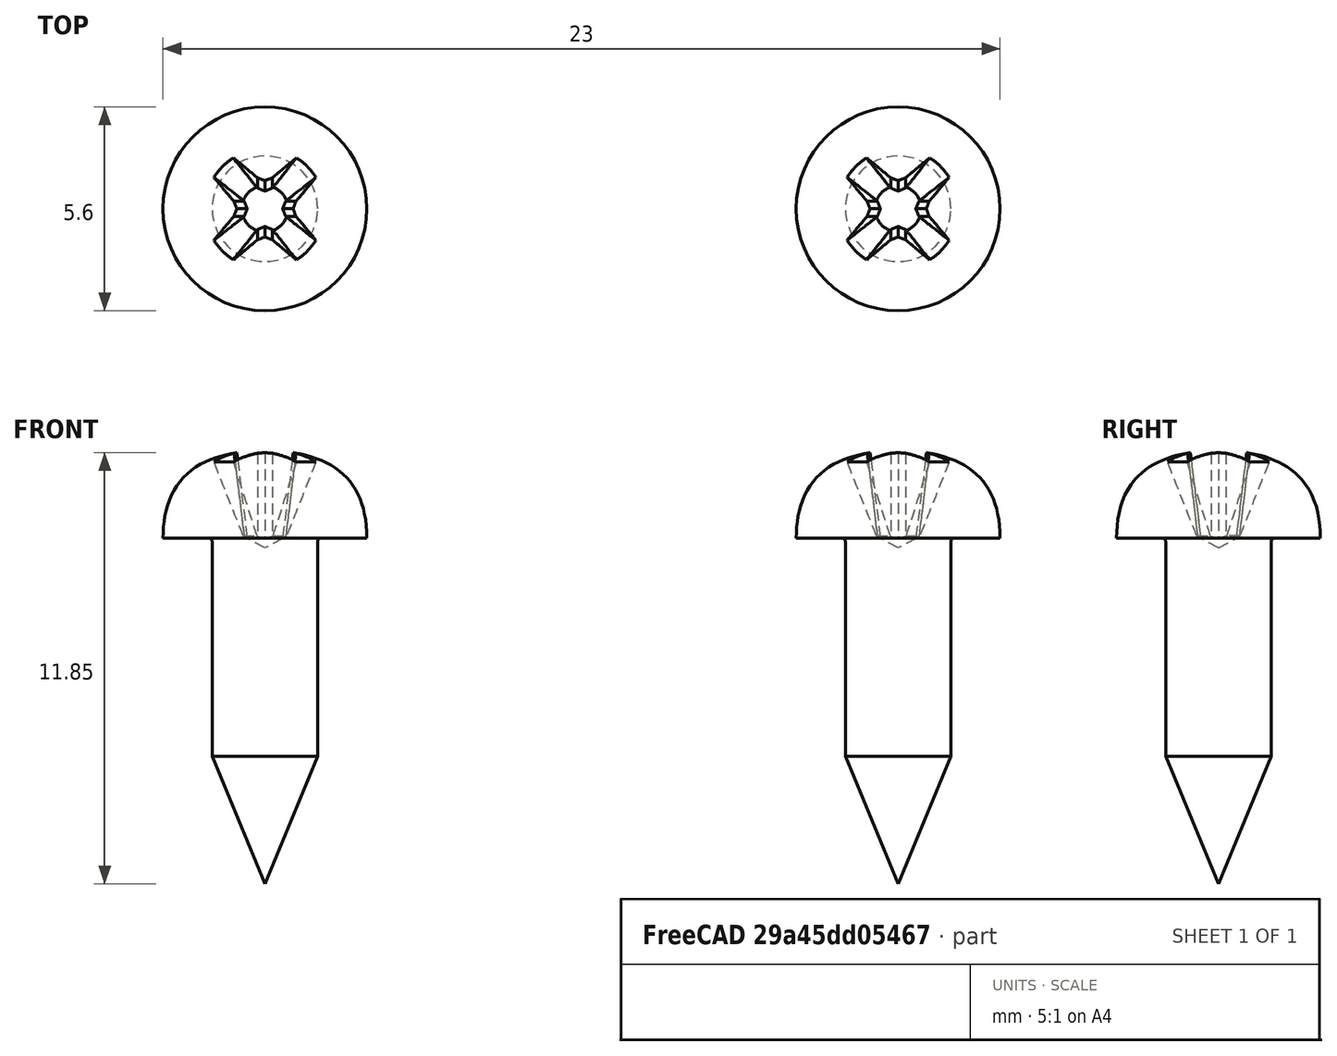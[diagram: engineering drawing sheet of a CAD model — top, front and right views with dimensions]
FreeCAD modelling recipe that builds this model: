
FCSTD DOCUMENT  (FreeCAD 1.0R39319 (Git))
Label: Assy_PiTracIRLED
License: All rights reserved
LicenseURL: https://en.wikipedia.org/wiki/All_rights_reserved
objects: TechDraw::DrawProjGroupItem×7, TechDraw::DrawViewBalloon×4, App::DocumentObjectGroup×3, App::Link×2, TechDraw::DrawSVGTemplate×2, Part::FeaturePython×2, TechDraw::DrawViewDimension×2, TechDraw::DrawPage×2, PartDesign::CoordinateSystem×1, App::FeaturePython×1, Spreadsheet::Sheet×1, TechDraw::DrawViewSpreadsheet×1, App::Part×1, TechDraw::DrawProjGroup×1
note: 6 computed .brp shape members not serialized (recipe doc carries the construction recipe); baked Part::Feature solids carry a one-line shape summary decoded from their .brp
EXTERNAL_REF file=../../Part/Print/5x2IRLED_Eyeball.FCStd obj=center
EXTERNAL_REF file=../../Part/Print/5x2IRLED_Eyeball.FCStd obj=Part
EXTERNAL_REF file=../../Part/Purchase/IRLED.FCStd obj=LCS_1
EXTERNAL_REF file=../../Part/Print/5x2IRLED_Eyeball.FCStd obj=LCS_1
EXTERNAL_REF file=../../Part/Purchase/IRLED.FCStd obj=IRLED_Only_1

FEATURE [App::DocumentObjectGroup] Parts
FEATURE [PartDesign::CoordinateSystem] LCS_Origin
  AttacherType = Attacher::AttachEngine3D
  AttachmentSupport = -> [X_Axis]
  MapMode = 2
FEATURE [App::DocumentObjectGroup] Constraints
FEATURE [App::FeaturePython] Variables  # WARN: FeaturePython — macro-defined, semantics opaque (R4)
  Type = App::PropertyContainer
FEATURE [App::DocumentObjectGroup] Configurations
FEATURE [App::Link] _x2IRLED_Eyeball  label="5x2IRLED_Eyeball"
  AttachedBy = #center
  AttachedTo = Parent Assembly#LCS_Origin
  LinkedObject = -> <external ../../Part/Print/5x2IRLED_Eyeball.FCStd>#Part
  SolverId = Asm4EE
  expr: Placement = LCS_Origin.Placement * AttachmentOffset * _x2IRLED_Eyeball#center.Placement ^ -1
FEATURE [App::Link] IRLED_Only_1  label="IRLED Only 1"
  AttachedBy = #LCS_1
  AttachedTo = _x2IRLED_Eyeball#LCS_1
  LinkPlacement = pos=(12.4672,17.5,0.0506) rot=(0,0,-1;1.5708rad)
  LinkedObject = -> <external ../../Part/Purchase/IRLED.FCStd>#IRLED_Only_1
  Placement = pos=(12.4672,17.5,0.0506) rot=(0,0,-1;1.5708rad)
  SolverId = Asm4EE
  expr: Placement = _x2IRLED_Eyeball.Placement * _x2IRLED_Eyeball#LCS_1.Placement * AttachmentOffset * IRLED#LCS_1.Placement ^ -1
FEATURE [TechDraw::DrawSVGTemplate] Template
  EditableTexts = approval_person=GitHub PR; creator=Stefan; date_of_issue=20.03.2026; document_type=Assembly Drawing; general_tolerances=na; identification_number=na; language_code=EN; part_material=na; revision_index=AAA; scale=1 : 1; sheet_number=1 / 1; title=Assy_PiTracIRLED
  Height = 297
  Orientation = 1
  Template = <userpath>/Documents/PiTrac/3D Printed Parts/Enclosure Version 3/Assets/PiTrac_A3_Landscape_ISO5457_minimal.svg
  Width = 420
FEATURE [Spreadsheet::Sheet] Spreadsheet  label="BOM"
  cells = A1=3; B1=2; C1='M3x10 mm self-tapping screw; D1='8-12 mm ; A2=2; B2=1; C2='5x2 IR LED board; D2='-; A3=1; B3=1; C3='5x2IRLED_Eyeball; D3='-; E3='PETG or PLA; A4='Position; B4='Quantity; C4='Part; D4='Dimensions; E4='Material
FEATURE [TechDraw::DrawViewSpreadsheet] Sheet
  CellEnd = E4
  CellStart = A1
  Font = osifont
  LineWidth = 0.35
  LockPosition = false
  Rotation = 0
  ScaleType = 2
  Source = -> Spreadsheet
  Symbol = <blob: 4584 chars omitted>
  TextSize = 12
  X = 324.475
  Y = 95.4404
FEATURE [Part::FeaturePython] Screw  label="ST2.9x9.5-Screw"  # WARN: FeaturePython — macro-defined, semantics opaque (R4)
  BaseObject = -> IRLED_Only_1 [Part__Feature067.Edge20]
  Diameter = 2
  Invert = false
  LeftHanded = false
  Length = 1
  LengthCustom = 9.5
  MatchOuter = false
  OffsetAngle = 0
  Placement = pos=(8.7,0,0.8124) rot=(0,0,1;0rad)
  Thread = false
  Type = 81
FEATURE [Part::FeaturePython] Screw001  label="ST2.9x9.5-Screw001"  # WARN: FeaturePython — macro-defined, semantics opaque (R4)
  BaseObject = -> IRLED_Only_1 [Part__Feature067.Edge17]
  Diameter = 2
  Invert = false
  LeftHanded = false
  Length = 1
  LengthCustom = 9.5
  MatchOuter = false
  OffsetAngle = 0
  Placement = pos=(-8.699,3.6e-15,0.8124) rot=(0,0,1;0rad)
  Thread = false
  Type = 81
FEATURE [App::Part] Assembly  label="Assy_PiTracIRLED"
  AssemblyType = Part::Link
  Group = -> [LCS_Origin,Constraints,Variables,Configurations,_x2IRLED_Eyeball,IRLED_Only_1,Screw,Screw001]
  Origin = -> Origin
  Type = Assembly
FEATURE [TechDraw::DrawProjGroupItem] ProjItem  label="Top"
  CoarseView = false
  Direction = (1,0,0)
  Focus = 100
  HardHidden = false
  IsoCount = 0
  IsoHidden = false
  IsoVisible = false
  LockPosition = false
  Perspective = false
  Rotation = 0
  RotationVector = (1,0,0)
  ScaleType = 0
  ScrubCount = 1
  SeamHidden = false
  SeamVisible = false
  SmoothHidden = false
  SmoothVisible = true
  Source = -> [Assembly]
  Type = 4
  X = 0
  XDirection = (0,-1,0)
  Y = -67
FEATURE [TechDraw::DrawProjGroupItem] View
  CoarseView = false
  Direction = (0.57735,-0.57735,0.57735)
  Focus = 100
  HardHidden = false
  IsoCount = 0
  IsoHidden = false
  IsoVisible = false
  LockPosition = false
  Perspective = false
  Rotation = 0
  RotationVector = (1,0,0)
  ScaleType = 0
  ScrubCount = 1
  SeamHidden = false
  SeamVisible = false
  SmoothHidden = false
  SmoothVisible = true
  Source = -> [Assembly]
  Type = 0
  X = 187.439
  XDirection = (-5.7735e-07,-0.707107,-0.707107)
  Y = 69.9551
FEATURE [TechDraw::DrawProjGroupItem] View001  label="Front"
  CoarseView = false
  Direction = (0,0,1)
  Focus = 100
  HardHidden = false
  IsoCount = 0
  IsoHidden = false
  IsoVisible = false
  LockPosition = true
  Perspective = false
  Rotation = 0
  RotationVector = (1,0,0)
  ScaleType = 2
  ScrubCount = 1
  SeamHidden = false
  SeamVisible = false
  SmoothHidden = false
  SmoothVisible = true
  Source = -> [Assembly]
  Type = 0
  X = 0
  XDirection = (0,-1,0)
  Y = 0
FEATURE [TechDraw::DrawProjGroupItem] ProjItem001  label="Top001"
  CoarseView = false
  Direction = (1,0,0)
  Focus = 100
  HardHidden = false
  IsoCount = 0
  IsoHidden = false
  IsoVisible = false
  LockPosition = false
  Perspective = false
  Rotation = 0
  RotationVector = (1,0,0)
  ScaleType = 0
  ScrubCount = 1
  SeamHidden = false
  SeamVisible = false
  SmoothHidden = false
  SmoothVisible = true
  Source = -> [Assembly]
  Type = 4
  X = 0
  XDirection = (0,-1,0)
  Y = -67
FEATURE [TechDraw::DrawProjGroupItem] ProjItem002  label="Left"
  CoarseView = false
  Direction = (0,1,1e-16)
  Focus = 100
  HardHidden = false
  IsoCount = 0
  IsoHidden = false
  IsoVisible = false
  LockPosition = false
  Perspective = false
  Rotation = 0
  RotationVector = (1,0,0)
  ScaleType = 0
  ScrubCount = 1
  SeamHidden = false
  SeamVisible = false
  SmoothHidden = false
  SmoothVisible = true
  Source = -> [Assembly]
  Type = 1
  X = 67
  XDirection = (0,-1e-16,1)
  Y = 0
FEATURE [TechDraw::DrawProjGroupItem] ProjItem003  label="Rear"
  CoarseView = false
  Direction = (0,0,-1)
  Focus = 100
  HardHidden = false
  IsoCount = 0
  IsoHidden = false
  IsoVisible = false
  LockPosition = false
  Perspective = false
  Rotation = 0
  RotationVector = (1,0,0)
  ScaleType = 0
  ScrubCount = 1
  SeamHidden = false
  SeamVisible = false
  SmoothHidden = false
  SmoothVisible = true
  Source = -> [Assembly]
  Type = 3
  X = 134
  XDirection = (0,1,0)
  Y = 0
FEATURE [TechDraw::DrawProjGroup] ProjGroup
  Anchor = -> View001
  AutoDistribute = true
  LockPosition = false
  ProjectionType = 0
  Rotation = 0
  ScaleType = 0
  Source = -> [Assembly]
  Views = -> [View001,ProjItem001,ProjItem002,ProjItem003]
  X = 92.1827
  Y = 215.347
  spacingX = 15
  spacingY = 15
FEATURE [TechDraw::DrawViewBalloon] Balloon
  BubbleShape = 0
  EndType = 0
  EndTypeScale = 1
  KinkLength = 5
  LockPosition = false
  OriginX = -28.2605
  OriginY = -17.3134
  Rotation = 0
  ScaleType = 0
  ShapeScale = 1
  SourceView = -> View001
  Text = 1
  TextWrapLen = -1
  X = -55
  Y = -28.23
FEATURE [TechDraw::DrawViewBalloon] Balloon001
  BubbleShape = 0
  EndType = 0
  EndTypeScale = 1
  KinkLength = 5
  LockPosition = false
  OriginX = -15.7268
  OriginY = 2.32286
  Rotation = 0
  ScaleType = 0
  ShapeScale = 1
  SourceView = -> View001
  Text = 2
  TextWrapLen = -1
  X = -55
  Y = 18.5627
FEATURE [TechDraw::DrawViewBalloon] Balloon002
  BubbleShape = 0
  EndType = 0
  EndTypeScale = 1
  KinkLength = 5
  LockPosition = false
  OriginX = -1.10408
  OriginY = -9.79311
  Rotation = 0
  ScaleType = 0
  ShapeScale = 1
  SourceView = -> View001
  Text = 3
  TextWrapLen = -1
  X = -55
  Y = -7.75816
FEATURE [TechDraw::DrawViewBalloon] Balloon003
  BubbleShape = 0
  EndType = 0
  EndTypeScale = 1
  KinkLength = 5
  LockPosition = false
  OriginX = -0.205
  OriginY = 9.27105
  Rotation = 0
  ScaleType = 0
  ShapeScale = 1
  SourceView = -> View001
  Text = 3
  TextWrapLen = -1
  X = -55
  Y = 39.7159
FEATURE [TechDraw::DrawViewDimension] Dimension
  AngleOverride = false
  Arbitrary = false
  ArbitraryTolerances = false
  BoxCorners = (2) [(-12,-40,-1e-07),(12,40,1e-07)]
  EqualTolerance = true
  ExtensionAngle = 0
  FormatSpec = %.2w
  FormatSpecOverTolerance = %+.2w
  FormatSpecUnderTolerance = %+.2w
  Inverted = false
  LineAngle = 0
  LockPosition = false
  MeasureType = 1
  OverTolerance = 0
  References2D = -> [ProjItem002]
  Rotation = 0
  ScaleType = 0
  TheoreticalExact = false
  Type = 0
  UnderTolerance = 0
  X = 0
  Y = 57.6927
FEATURE [TechDraw::DrawViewDimension] Dimension001
  AngleOverride = false
  Arbitrary = false
  ArbitraryTolerances = false
  BoxCorners = (2) [(-40,-40,0),(40,40,0)]
  EqualTolerance = true
  ExtensionAngle = 0
  FormatSpec = ⌀%.2w
  FormatSpecOverTolerance = %+.2w
  FormatSpecUnderTolerance = %+.2w
  Inverted = false
  LineAngle = 0
  LockPosition = false
  MeasureType = 1
  OverTolerance = 0
  References2D = -> [ProjItem003]
  Rotation = 0
  ScaleType = 0
  TheoreticalExact = false
  Type = 5
  UnderTolerance = 0
  X = 65.2263
  Y = 46.4264
FEATURE [TechDraw::DrawPage] Page
  KeepUpdated = true
  NextBalloonIndex = 8
  ProjectionType = 0
  Template = -> Template
  Views = -> [Sheet,View,ProjGroup,Balloon,Balloon001,Balloon002,Balloon003,Dimension,Dimension001]
FEATURE [TechDraw::DrawSVGTemplate] Template001
  Height = 210
  Orientation = 1
  Template = C:/Program Files/FreeCAD 1.0/data/Mod/TechDraw/Templates/Default_Template_A4_Landscape.svg
  Width = 297
FEATURE [TechDraw::DrawProjGroupItem] View002
  CoarseView = false
  Direction = (0.57735,-0.57735,0.57735)
  Focus = 100
  HardHidden = false
  IsoCount = 0
  IsoHidden = false
  IsoVisible = false
  LockPosition = false
  Perspective = false
  Rotation = 0
  RotationVector = (1,0,0)
  Scale = 2
  ScaleType = 2
  ScrubCount = 1
  SeamHidden = false
  SeamVisible = false
  SmoothHidden = false
  SmoothVisible = true
  Source = -> [Assembly]
  Type = 0
  X = 148.5
  XDirection = (-5.7735e-07,-0.707107,-0.707107)
  Y = 105
FEATURE [TechDraw::DrawPage] Page001
  KeepUpdated = true
  NextBalloonIndex = 1
  ProjectionType = 0
  Template = -> Template001
  Views = -> [View002]

RESOLVED EXTERNAL PARTS (link-assembly join: the EXTERNAL_REF files above that resolve inside this repo's crawl, each included once):
---- part ../../Part/Print/5x2IRLED_Eyeball.FCStd = doc fcstd_bd1177192a88 ----
FCSTD DOCUMENT  (FreeCAD 1.0R39319 (Git))
Label: 5x2IRLED_Eyeball
License: All rights reserved
LicenseURL: https://en.wikipedia.org/wiki/All_rights_reserved
objects: Sketcher::SketchObject×9, PartDesign::Pocket×5, PartDesign::Fillet×4, PartDesign::Pad×3, PartDesign::Mirrored×2, PartDesign::CoordinateSystem×2, PartDesign::Revolution×1, PartDesign::Body×1, App::Part×1
note: 64 computed .brp shape members not serialized (recipe doc carries the construction recipe); baked Part::Feature solids carry a one-line shape summary decoded from their .brp

FEATURE [Sketcher::SketchObject] Sketch
  ArcFitTolerance = 1e-06
  AttachmentSupport = -> [YZ_Plane001]
  FullyConstrained = true
  MakeInternals = false
  MapMode = 5
  Placement = pos=(0,0,0) rot=(0.57735,0.57735,0.57735;2.0944rad)
  sketch-geometry (9):
    g0: ArcOfCircle CenterX=0 CenterY=0 CenterZ=0 NormalX=0 NormalY=0 NormalZ=1 AngleXU=0 Radius=40 StartAngle=5.97849 EndAngle=6.58788
    g1: LineSegment StartX=38.1576 StartY=12 StartZ=0 EndX=37.5671 EndY=12 EndZ=0
    g2: LineSegment StartX=37.5671 StartY=12 StartZ=0 EndX=23 EndY=1.8 EndZ=0
    g3: LineSegment StartX=23 StartY=1.8 StartZ=0 EndX=0 EndY=1.8 EndZ=0
    g4: LineSegment StartX=0 StartY=1.8 StartZ=0 EndX=0 EndY=-3.2 EndZ=0
    g5: LineSegment StartX=0 StartY=-3.2 StartZ=0 EndX=23 EndY=-3.2 EndZ=0
    g6: LineSegment StartX=23 StartY=-3.2 StartZ=0 EndX=35.5677 EndY=-12 EndZ=0
    g7: LineSegment StartX=35.5677 StartY=-12 StartZ=0 EndX=38.1576 EndY=-12 EndZ=0
    g8: LineSegment [constr] StartX=23 StartY=1.8 StartZ=0 EndX=23 EndY=-3.2 EndZ=0
  constraints (26):
    c: Coincident(g0,g-1)
    c: Radius(g0) = 40
    c: Coincident(g0,g1)
    c: Horizontal(g1)
    c: Coincident(g1,g2)
    c: Coincident(g2,g3)
    c: PointOnObject(g3,g-2)
    c: Horizontal(g3)
    c: Coincident(g3,g4)
    c: PointOnObject(g4,g-2)
    c: Coincident(g4,g5)
    c: Horizontal(g5)
    c: Coincident(g5,g6)
    c: Coincident(g6,g7)
    c: Coincident(g7,g0)
    c: Horizontal(g7)
    c: Distance(g7,g1) = 24
    c: DistanceX(g3,g3) = 23
    c: Coincident(g8,g2)
    c: Coincident(g8,g5)
    c: Vertical(g8)
    c: Distance(g5,g3) = 5
    c: Angle(g6,g7) = 0.610865
    c: Angle(g3,g2) = 0.610865
    c: Distance(g3,g-1) = 1.8
    c: Distance(g1,g-1) = 12
FEATURE [PartDesign::Revolution] Revolution
  Angle = 360
  Angle2 = 60
  Axis = (0,0,1)
  Base = (0,0,0)
  Placement = pos=(0,0,0) rot=(1,1,1;2.0944rad)
  Profile = -> Sketch
  ReferenceAxis = -> Sketch [V_Axis]
  Refine = true
  Reversed = true
  Suppressed = false
  Type = 0
FEATURE [Sketcher::SketchObject] Sketch001
  ArcFitTolerance = 1e-06
  AttachmentSupport = -> [Revolution]
  FullyConstrained = true
  MakeInternals = false
  MapMode = 5
  Placement = pos=(-4e-16,0,1.8) rot=(0,0,-1;1.5708rad)
  sketch-geometry (4):
    g0: LineSegment StartX=-18 StartY=13 StartZ=0 EndX=-18 EndY=-13 EndZ=0
    g1: LineSegment StartX=-18 StartY=-13 StartZ=0 EndX=18 EndY=-13 EndZ=0
    g2: LineSegment StartX=18 StartY=-13 StartZ=0 EndX=18 EndY=13 EndZ=0
    g3: LineSegment StartX=18 StartY=13 StartZ=0 EndX=-18 EndY=13 EndZ=0
  constraints (10):
    c: Coincident(g0,g1)
    c: Coincident(g1,g2)
    c: Coincident(g2,g3)
    c: Coincident(g3,g0)
    c: Vertical(g2)
    c: Horizontal(g1)
    c: Distance(g2,g0) = 36
    c: Distance(g3,g1) = 26
    c: Symmetric(g0,g2,g-2)
    c: Symmetric(g0,g0,g-1)
FEATURE [PartDesign::Pocket] Pocket
  BaseFeature = -> Revolution
  Direction = (0,0,-1)
  Length = 1.8
  Length2 = 5
  Placement = pos=(0,0,0) rot=(1,1,1;2.0944rad)
  Profile = -> Sketch001
  ReferenceAxis = -> Sketch001 [N_Axis]
  Refine = true
  Suppressed = false
  Type = 0
FEATURE [Sketcher::SketchObject] Sketch002
  ArcFitTolerance = 1e-06
  AttachmentSupport = -> [Pocket]
  ExternalGeometry = -> [Pocket]
  FullyConstrained = true
  MakeInternals = false
  MapMode = 5
  Placement = pos=(0,0,-4.4e-15) rot=(0,0,-1;1.5708rad)
  sketch-geometry (5):
    g0: LineSegment StartX=-16.5 StartY=11.5 StartZ=0 EndX=-16.5 EndY=-11.5 EndZ=0
    g1: LineSegment StartX=-16.5 StartY=-11.5 StartZ=0 EndX=16.5 EndY=-11.5 EndZ=0
    g2: LineSegment StartX=16.5 StartY=-11.5 StartZ=0 EndX=16.5 EndY=11.5 EndZ=0
    g3: LineSegment StartX=16.5 StartY=11.5 StartZ=0 EndX=-16.5 EndY=11.5 EndZ=0
    g4: Circle [constr] CenterX=13.5 CenterY=0 CenterZ=0 NormalX=0 NormalY=0 NormalZ=1 AngleXU=0 Radius=2.5
  constraints (15):
    c: Coincident(g0,g1)
    c: Coincident(g1,g2)
    c: Coincident(g2,g3)
    c: Coincident(g3,g0)
    c: Vertical(g0)
    c: Vertical(g2)
    c: Horizontal(g1)
    c: Horizontal(g3)
    c: Distance(g0,g-6) = 1.5
    c: Distance(g-4,g2) = 1.5
    c: Distance(g-3,g3) = 1.5
    c: Distance(g-5,g1) = 1.5
    c: PointOnObject(g4,g-1)
    c: DistanceX(g-1,g4) = 13.5
    c: Diameter(g4) = 5
FEATURE [PartDesign::Pocket] Pocket001
  BaseFeature = -> Pocket
  Direction = (0,0,-1)
  Length = 5
  Length2 = 5
  Placement = pos=(0,0,0) rot=(1,1,1;2.0944rad)
  Profile = -> Sketch002
  ReferenceAxis = -> Sketch002 [N_Axis]
  Refine = true
  Suppressed = false
  Type = 1
FEATURE [Sketcher::SketchObject] Sketch003
  ArcFitTolerance = 1e-06
  AttachmentSupport = -> [Pocket001]
  ExternalGeometry = -> [Pocket001]
  FullyConstrained = true
  MakeInternals = false
  MapMode = 5
  Placement = pos=(0,0,-4.4e-15) rot=(0,0,-1;1.5708rad)
  sketch-geometry (4):
    g0: LineSegment StartX=3 StartY=35.441 StartZ=0 EndX=3 EndY=8.7 EndZ=0
    g1: ArcOfCircle CenterX=0 CenterY=8.7 CenterZ=0 NormalX=0 NormalY=0 NormalZ=1 AngleXU=0 Radius=3 StartAngle=3.14159 EndAngle=6.28319
    g2: LineSegment StartX=-3 StartY=8.7 StartZ=0 EndX=-3 EndY=35.441 EndZ=0
    g3: ArcOfCircle CenterX=5.6e-15 CenterY=6.38282e-05 CenterZ=0 NormalX=0 NormalY=0 NormalZ=1 AngleXU=0 Radius=35.5676 StartAngle=1.48635 EndAngle=1.65524
  constraints (12):
    c: Vertical(g0)
    c: Tangent(g0,g1) = 1.5708
    c: Tangent(g1,g2) = 1.5708
    c: Vertical(g2)
    c: Radius(g1) = 3
    c: DistanceY(g-1,g1) = 8.7
    c: PointOnObject(g1,g-2)
    c: Coincident(g3,g2)
    c: Coincident(g3,g0)
    c: Tangent(g3,g-3)
    c: PointOnObject(g0,g-3)
    c: PointOnObject(g2,g-3)
FEATURE [PartDesign::Pad] Pad
  BaseFeature = -> Pocket001
  Direction = (0,0,1)
  Length = 10
  Length2 = 10
  Placement = pos=(0,0,0) rot=(1,1,1;2.0944rad)
  Profile = -> Sketch003
  ReferenceAxis = -> Sketch003 [N_Axis]
  Refine = true
  Reversed = true
  Suppressed = false
  Type = 3
  UpToFace = -> Pocket001 [Face2]
FEATURE [PartDesign::Mirrored] Mirrored
  BaseFeature = -> Pad
  MirrorPlane = -> YZ_Plane001
  Originals = -> [Pad]
  Placement = pos=(0,0,0) rot=(1,1,1;2.0944rad)
  Refine = true
  Suppressed = false
  TransformMode = 0
FEATURE [PartDesign::Fillet] Fillet
  Base = -> Mirrored [Edge68,Edge65,Edge56,Edge46]
  BaseFeature = -> Mirrored
  Placement = pos=(0,0,0) rot=(1,1,1;2.0944rad)
  Radius = 3
  Refine = true
  SupportTransform = false
  Suppressed = false
  UseAllEdges = false
FEATURE [PartDesign::Fillet] Fillet001
  Base = -> Fillet [Edge64,Edge63,Edge68,Edge66]
  BaseFeature = -> Fillet
  Placement = pos=(0,0,0) rot=(1,1,1;2.0944rad)
  Radius = 1
  Refine = true
  SupportTransform = false
  Suppressed = false
  UseAllEdges = false
FEATURE [Sketcher::SketchObject] Sketch004
  ArcFitTolerance = 1e-06
  AttachmentSupport = -> [Fillet001]
  ExternalGeometry = -> [Fillet001]
  FullyConstrained = true
  MakeInternals = false
  MapMode = 5
  Placement = pos=(0,0,-4.4e-15) rot=(0,0,-1;1.5708rad)
  sketch-geometry (2):
    g0: Circle CenterX=0 CenterY=8.7 CenterZ=0 NormalX=0 NormalY=0 NormalZ=1 AngleXU=0 Radius=1.1
    g1: Circle CenterX=0 CenterY=-8.7 CenterZ=0 NormalX=0 NormalY=0 NormalZ=1 AngleXU=0 Radius=1.1
  constraints (4):
    c: Coincident(g0,g-3)
    c: Coincident(g1,g-4)
    c: Diameter(g0) = 2.2
    c: Diameter(g1) = 2.2
FEATURE [PartDesign::Pocket] Pocket002
  BaseFeature = -> Fillet001
  Direction = (0,0,-1)
  Length = 5
  Length2 = 5
  Placement = pos=(0,0,0) rot=(1,1,1;2.0944rad)
  Profile = -> Sketch004
  ReferenceAxis = -> Sketch004 [N_Axis]
  Refine = true
  Suppressed = false
  Type = 1
FEATURE [Sketcher::SketchObject] Sketch005
  ArcFitTolerance = 1e-06
  AttachmentSupport = -> [Pocket002]
  ExternalGeometry = -> [Pocket002]
  FullyConstrained = true
  MakeInternals = false
  MapMode = 5
  Placement = pos=(2.6e-15,0,-12) rot=(0.707107,0.707107,0;3.14159rad)
  sketch-geometry (6):
    g0: LineSegment StartX=35.5677 StartY=-1.363e-13 StartZ=0 EndX=24.75 EndY=-1.363e-13 EndZ=0
    g1: ArcOfCircle CenterX=23 CenterY=0 CenterZ=0 NormalX=0 NormalY=0 NormalZ=1 AngleXU=0 Radius=1.75 StartAngle=1.0472 EndAngle=6.28319
    g2: LineSegment StartX=23.875 StartY=1.51554 StartZ=0 EndX=25 EndY=3.4641 EndZ=0
    g3: ArcOfCircle CenterX=23 CenterY=0 CenterZ=0 NormalX=0 NormalY=0 NormalZ=1 AngleXU=0 Radius=4 StartAngle=1.0472 EndAngle=4.71239
    g4: LineSegment StartX=23 StartY=-4 StartZ=0 EndX=35.3421 EndY=-4 EndZ=0
    g5: ArcOfCircle CenterX=9.30302e-06 CenterY=-5.24781e-07 CenterZ=0 NormalX=0 NormalY=0 NormalZ=1 AngleXU=0 Radius=35.5677 StartAngle=6.17049 EndAngle=6.28319
  constraints (17):
    c: Horizontal(g0)
    c: Perpendicular(g0,g1) = 4.71239
    c: Coincident(g1,g2)
    c: Perpendicular(g2,g3) = 1.5708
    c: Horizontal(g4)
    c: Coincident(g1,g3)
    c: PointOnObject(g0,g-3)
    c: PointOnObject(g4,g-3)
    c: Radius(g1) = 1.75
    c: Radius(g3) = 4
    c: PointOnObject(g1,g-1)
    c: Tangent(g3,g4) = -1.5708
    c: Angle(g0,g2) = 1.0472
    c: DistanceX(g-1,g1) = 23
    c: Coincident(g5,g0)
    c: Coincident(g5,g4)
    c: Tangent(g5,g-3)
FEATURE [PartDesign::Pad] Pad001
  BaseFeature = -> Pocket002
  Direction = (1.7e-15,0,-1)
  Length = 3
  Length2 = 10
  Placement = pos=(0,0,0) rot=(1,1,1;2.0944rad)
  Profile = -> Sketch005
  ReferenceAxis = -> Sketch005 [N_Axis]
  Refine = true
  Reversed = true
  Suppressed = false
  Type = 0
FEATURE [Sketcher::SketchObject] Sketch006
  ArcFitTolerance = 1e-06
  AttachmentSupport = -> [Pad001]
  ExternalGeometry = -> [Pad001]
  FullyConstrained = true
  MakeInternals = false
  MapMode = 5
  Placement = pos=(1.55e-14,0,-9) rot=(0,0,-1;1.5708rad)
  sketch-geometry (4):
    g0: LineSegment StartX=-24.75 StartY=-1.246e-13 StartZ=0 EndX=-31.2833 EndY=-1.228e-13 EndZ=0
    g1: ArcOfCircle CenterX=-4.4234e-12 CenterY=-1.386e-13 CenterZ=0 NormalX=0 NormalY=0 NormalZ=1 AngleXU=0 Radius=31.2833 StartAngle=3.14159 EndAngle=3.26981
    g2: LineSegment StartX=-31.0265 StartY=-4 StartZ=0 EndX=-24.4246 EndY=-4 EndZ=0
    g3: ArcOfCircle CenterX=-4.4234e-12 CenterY=-1.386e-13 CenterZ=0 NormalX=0 NormalY=0 NormalZ=1 AngleXU=0 Radius=24.75 StartAngle=3.14159 EndAngle=3.30392
  constraints (9):
    c: Coincident(g-4,g0)
    c: Coincident(g0,g-4)
    c: Perpendicular(g0,g1) = 1.5708
    c: Coincident(g1,g-5)
    c: Coincident(g1,g2)
    c: PointOnObject(g2,g-5)
    c: Coincident(g3,g2)
    c: Coincident(g3,g0)
    c: Coincident(g3,g1)
FEATURE [PartDesign::Pad] Pad002
  BaseFeature = -> Pad001
  Direction = (-2e-15,0,1)
  Length = 10
  Length2 = 10
  Placement = pos=(0,0,0) rot=(1,1,1;2.0944rad)
  Profile = -> Sketch006
  ReferenceAxis = -> Sketch006 [N_Axis]
  Refine = true
  Suppressed = false
  Type = 3
  UpToFace = -> Pad001 [Face33]
FEATURE [PartDesign::Mirrored] Mirrored001
  BaseFeature = -> Pad002
  MirrorPlane = -> XZ_Plane001
  Originals = -> [Pad001,Pad002]
  Placement = pos=(0,0,0) rot=(1,1,1;2.0944rad)
  Refine = true
  Suppressed = false
  TransformMode = 0
FEATURE [PartDesign::Fillet] Fillet002
  Base = -> Mirrored001 [Edge90,Edge5]
  BaseFeature = -> Mirrored001
  Placement = pos=(0,0,0) rot=(1,1,1;2.0944rad)
  Radius = 1
  Refine = true
  SupportTransform = false
  Suppressed = false
  UseAllEdges = false
FEATURE [Sketcher::SketchObject] Sketch007
  ArcFitTolerance = 1e-06
  AttachmentSupport = -> [Fillet002]
  ExternalGeometry = -> [Fillet002]
  FullyConstrained = true
  MakeInternals = false
  MapMode = 5
  Placement = pos=(-4e-16,0,1.8) rot=(0,0,-1;1.5708rad)
  sketch-geometry (4):
    g0: LineSegment StartX=-5 StartY=-13 StartZ=0 EndX=-5 EndY=-14.5 EndZ=0
    g1: LineSegment StartX=-5 StartY=-14.5 StartZ=0 EndX=5 EndY=-14.5 EndZ=0
    g2: LineSegment StartX=5 StartY=-14.5 StartZ=0 EndX=5 EndY=-13 EndZ=0
    g3: LineSegment StartX=5 StartY=-13 StartZ=0 EndX=-5 EndY=-13 EndZ=0
  constraints (11):
    c: Coincident(g0,g1)
    c: Coincident(g1,g2)
    c: Coincident(g2,g3)
    c: Coincident(g3,g0)
    c: Vertical(g0)
    c: Vertical(g2)
    c: Horizontal(g1)
    c: PointOnObject(g0,g-3)
    c: Distance(g2,g0) = 10
    c: Distance(g3,g1) = 1.5
    c: Symmetric(g0,g2,g-2)
FEATURE [PartDesign::Pocket] Pocket003
  BaseFeature = -> Fillet002
  Direction = (2.3e-15,0,-1)
  Length = 0
  Length2 = 5
  Placement = pos=(0,0,0) rot=(1,1,1;2.0944rad)
  Profile = -> Sketch007
  ReferenceAxis = -> Sketch007 [N_Axis]
  Refine = true
  Suppressed = false
  Type = 3
  UpToFace = -> Fillet002 [Face30]
FEATURE [PartDesign::Fillet] Fillet003
  Base = -> Pocket003 [Edge154,Edge157]
  BaseFeature = -> Pocket003
  Placement = pos=(0,0,0) rot=(1,1,1;2.0944rad)
  Radius = 1
  Refine = true
  SupportTransform = false
  Suppressed = false
  UseAllEdges = false
FEATURE [Sketcher::SketchObject] Sketch008
  ArcFitTolerance = 1e-06
  AttachmentSupport = -> [Fillet003]
  ExternalGeometry = -> [Fillet003]
  FullyConstrained = true
  MakeInternals = false
  MapMode = 5
  Placement = pos=(2.6e-15,0,-12) rot=(0.707107,0.707107,0;3.14159rad)
  sketch-geometry (20):
    g0: LineSegment StartX=-30.25 StartY=-1.75 StartZ=0 EndX=-30.25 EndY=-0.75 EndZ=0
    g1: LineSegment StartX=-30.25 StartY=-0.75 StartZ=0 EndX=-29.75 EndY=-0.75 EndZ=0
    g2: LineSegment StartX=-29.75 StartY=-0.75 StartZ=0 EndX=-29.75 EndY=-1.75 EndZ=0
    g3: LineSegment StartX=-29.75 StartY=-1.75 StartZ=0 EndX=-28.75 EndY=-1.75 EndZ=0
    g4: LineSegment StartX=-28.75 StartY=-1.75 StartZ=0 EndX=-28.75 EndY=-2.25 EndZ=0
    g5: LineSegment StartX=-28.75 StartY=-2.25 StartZ=0 EndX=-29.75 EndY=-2.25 EndZ=0
    g6: LineSegment StartX=-29.75 StartY=-2.25 StartZ=0 EndX=-29.75 EndY=-3.25 EndZ=0
    g7: LineSegment StartX=-29.75 StartY=-3.25 StartZ=0 EndX=-30.25 EndY=-3.25 EndZ=0
    g8: LineSegment StartX=-30.25 StartY=-3.25 StartZ=0 EndX=-30.25 EndY=-2.25 EndZ=0
    g9: LineSegment StartX=-30.25 StartY=-2.25 StartZ=0 EndX=-31.25 EndY=-2.25 EndZ=0
    g10: LineSegment StartX=-31.25 StartY=-2.25 StartZ=0 EndX=-31.25 EndY=-1.75 EndZ=0
    g11: LineSegment StartX=-31.25 StartY=-1.75 StartZ=0 EndX=-30.25 EndY=-1.75 EndZ=0
    g12: LineSegment [constr] StartX=-31.25 StartY=-2 StartZ=0 EndX=-28.75 EndY=-2 EndZ=0
    g13: LineSegment [constr] StartX=-30 StartY=-0.75 StartZ=0 EndX=-30 EndY=-3.25 EndZ=0
    g14: LineSegment StartX=28.75 StartY=-1.75 StartZ=0 EndX=28.75 EndY=-2.25 EndZ=0
    g15: LineSegment StartX=28.75 StartY=-2.25 StartZ=0 EndX=31.25 EndY=-2.25 EndZ=0
    g16: LineSegment StartX=31.25 StartY=-2.25 StartZ=0 EndX=31.25 EndY=-1.75 EndZ=0
    g17: LineSegment StartX=31.25 StartY=-1.75 StartZ=0 EndX=28.75 EndY=-1.75 EndZ=0
    g18: LineSegment [constr] StartX=30 StartY=-1.75 StartZ=0 EndX=30 EndY=-2.25 EndZ=0
    g19: LineSegment [constr] StartX=28.75 StartY=-2 StartZ=0 EndX=31.25 EndY=-2 EndZ=0
  constraints (54):
    c: Vertical(g0)
    c: Coincident(g0,g1)
    c: Horizontal(g1)
    c: Coincident(g1,g2)
    c: Vertical(g2)
    c: Coincident(g2,g3)
    c: Horizontal(g3)
    c: Coincident(g3,g4)
    c: Coincident(g4,g5)
    c: Coincident(g5,g6)
    c: Vertical(g6)
    c: Coincident(g6,g7)
    c: Coincident(g7,g8)
    c: Vertical(g8)
    c: Coincident(g8,g9)
    c: Horizontal(g9)
    c: Coincident(g9,g10)
    c: Coincident(g10,g11)
    c: Coincident(g11,g0)
    c: Horizontal(g11)
    c: Horizontal(g5)
    c: Horizontal(g7)
    c: Vertical(g10)
    c: Vertical(g4)
    c: Symmetric(g10,g10,g12)
    c: Symmetric(g4,g4,g12)
    c: Horizontal(g12)
    c: Symmetric(g1,g1,g13)
    c: Symmetric(g7,g7,g13)
    c: Vertical(g13)
    c: Symmetric(g10,g3,g13)
    c: Symmetric(g7,g0,g12)
    c: DistanceX(g12,g12) = 2.5
    c: DistanceY(g13,g13) = 2.5
    c: Distance(g11,g9) = 0.5
    c: Distance(g2,g0) = 0.5
    c: Distance(g-3,g12) = 2
    c: Distance(g-2,g13) = 30
    c: Coincident(g14,g15)
    c: Coincident(g15,g16)
    c: Coincident(g16,g17)
    c: Coincident(g17,g14)
    c: Vertical(g14)
    c: Vertical(g16)
    c: Horizontal(g15)
    c: Horizontal(g17)
    c: Symmetric(g17,g17,g18)
    c: Symmetric(g15,g15,g18)
    c: Symmetric(g14,g14,g19)
    c: Symmetric(g16,g16,g19)
    c: DistanceY(g16,g16) = 0.5
    c: DistanceX(g17,g17) = 2.5
    c: Distance(g-1,g19) = 2
    c: Distance(g-2,g18) = 30
FEATURE [PartDesign::Pocket] Pocket004
  BaseFeature = -> Fillet003
  Direction = (0,0,1)
  Length = 1
  Length2 = 5
  Placement = pos=(0,0,0) rot=(1,1,1;2.0944rad)
  Profile = -> Sketch008
  ReferenceAxis = -> Sketch008 [N_Axis]
  Refine = true
  Suppressed = false
  Type = 0
FEATURE [PartDesign::Body] Body  label="5x2IRLED_Eyeball001"
  AllowCompound = false
  Group = -> [Sketch,Revolution,Sketch001,Pocket,Sketch002,Pocket001,Sketch003,Pad,Mirrored,Fillet,Fillet001,Sketch004,Pocket002,Sketch005,Pad001,Sketch006,Pad002,Mirrored001,Fillet002,Sketch007,Pocket003,Fillet003,Sketch008,Pocket004]
  Origin = -> Origin001
  Tip = -> Pocket004
FEATURE [PartDesign::CoordinateSystem] center
  AttacherType = Attacher::AttachEngine3D
FEATURE [PartDesign::CoordinateSystem] LCS_1
  AttacherType = Attacher::AttachEngine3D
  AttachmentSupport = -> [Pocket004]
  MapMode = 11
  Placement = pos=(8.7,0,-4e-15) rot=(0,0,1;0rad)
FEATURE [App::Part] Part  label="5x2IRLED_Eyeball"
  Group = -> [Body,center,LCS_1]
  Origin = -> Origin
